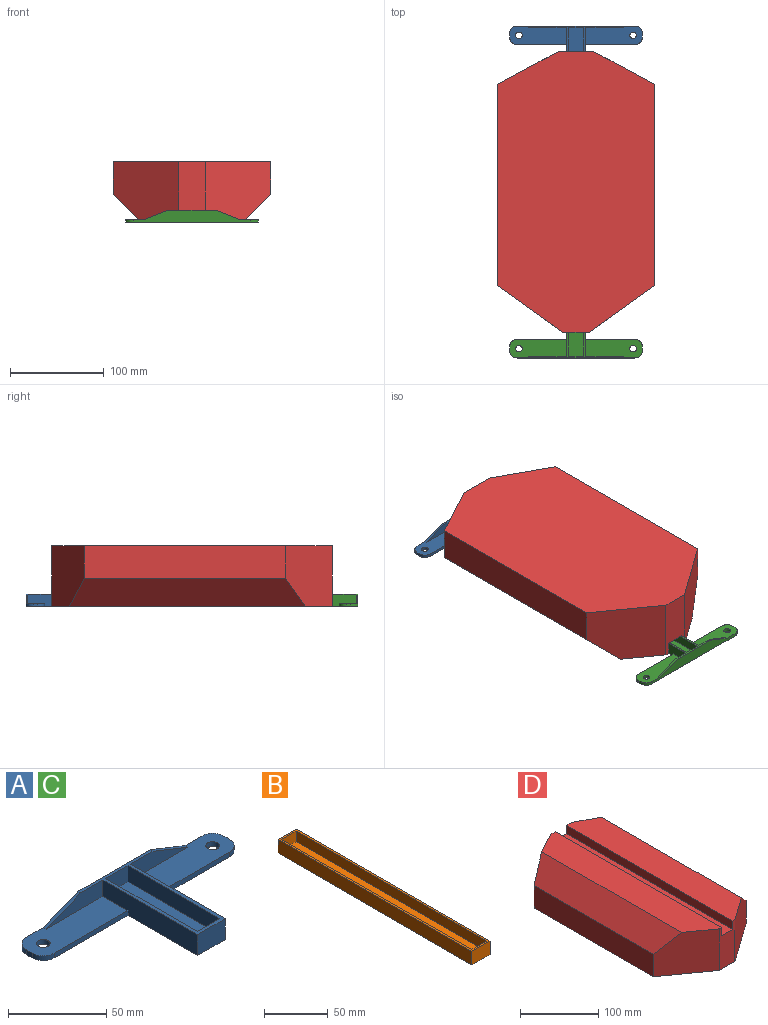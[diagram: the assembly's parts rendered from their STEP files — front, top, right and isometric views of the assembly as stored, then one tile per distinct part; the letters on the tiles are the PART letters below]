
ASSEMBLY  parts=4 mates=3
PART A: 27 faces, bbox 142x70x13 mm
  f0: plane 61x20mm, normal (0,0,1), area 1072mm2, adj f4,f5,f6,f7,f10,f15,f16,f18
  f1: plane 53x3mm, normal (0,-1,0), area 159mm2, adj f2,f11,f12,f14
  f2: plane 68x13mm, normal (-1,0,0), area 830mm2, adj f1,f3,f11,f12,f17,f23
  f3: plane 20x13mm, normal (0,-1,0), area 260mm2, adj f2,f4,f12,f23
  f4: plane 68x13mm, normal (1,0,0), area 830mm2, adj f0,f3,f5,f12,f18,f23
  f5: plane 53x3mm, normal (0,-1,0), area 159mm2, adj f0,f4,f12,f15
  f6: plane 4x3mm, normal (1,0,0), area 12mm2, adj f0,f12,f15,f16
  f7: plane 126x13mm, normal (0,1,0), area 1148mm2, adj f0,f11,f12,f13,f16,f23,f25,f26
  f8: cylinder r=3.5mm len=7mm, axis (0,0,-1), area 66mm2, adj f11,f12
  f9: plane 4x3mm, normal (-1,0,0), area 12mm2, adj f11,f12,f13,f14
  f10: cylinder r=3.5mm len=7mm, axis (0,0,-1), area 66mm2, adj f0,f12
  f11: plane 61x20mm, normal (0,0,1), area 1072mm2, adj f1,f2,f7,f8,f9,f13,f14,f17
  f12: plane 142x70mm, normal (0,0,-1), area 3708.1mm2, adj f1,f2,f3,f4,f5,f6,f7,f8
  f13: cylinder r=8mm len=8mm, axis (0,0,-1), area 37.7mm2, adj f7,f9,f11,f12
  f14: cylinder r=8mm len=8mm, axis (0,0,1), area 37.7mm2, adj f1,f9,f11,f12
  f15: cylinder r=8mm len=8mm, axis (0,0,1), area 37.7mm2, adj f0,f5,f6,f12
  f16: cylinder r=8mm len=8mm, axis (0,0,1), area 37.7mm2, adj f0,f6,f7,f12
  f17: plane 41x10mm, normal (0,-1,0), area 285mm2, adj f2,f11,f23,f26
  f18: plane 41x10mm, normal (0,-1,0), area 285mm2, adj f0,f4,f23,f25
  f19: plane 66x10mm, normal (1,0,0), area 660mm2, adj f20,f22,f23,f24
  f20: plane 16x10mm, normal (0,-1,0), area 160mm2, adj f19,f21,f23,f24
  f21: plane 66x10mm, normal (-1,0,0), area 660mm2, adj f20,f22,f23,f24
  f22: plane 16x10mm, normal (0,1,0), area 160mm2, adj f19,f21,f23,f24
  f23: plane 70x52mm, normal (0,0,1), area 408mm2, adj f2,f3,f4,f7,f17,f18,f19,f20
  f24: plane 66x16mm, normal (0,0,1), area 1056mm2, adj f19,f20,f21,f22
  f25: plane 25x10mm, normal (0.37,0,0.93), area 53.9mm2, adj f0,f7,f18,f23
  f26: plane 25x10mm, normal (-0.37,0,0.93), area 53.9mm2, adj f7,f11,f17,f23
PART B: 11 faces, bbox 20x215x13 mm
  f0: plane 215x13mm, normal (1,0,0), area 2795mm2, adj f1,f3,f4,f9
  f1: plane 20x13mm, normal (0,1,0), area 260mm2, adj f0,f2,f4,f9
  f2: plane 215x13mm, normal (-1,0,0), area 2795mm2, adj f1,f3,f4,f9
  f3: plane 20x13mm, normal (0,-1,0), area 260mm2, adj f0,f2,f4,f9
  f4: plane 215x20mm, normal (0,0,-1), area 4300mm2, adj f0,f1,f2,f3
  f5: plane 16x10mm, normal (0,-1,0), area 160mm2, adj f6,f8,f9,f10
  f6: plane 211x10mm, normal (-1,0,0), area 2110mm2, adj f5,f7,f9,f10
  f7: plane 16x10mm, normal (0,1,0), area 160mm2, adj f6,f8,f9,f10
  f8: plane 211x10mm, normal (1,0,0), area 2110mm2, adj f5,f7,f9,f10
  f9: plane 215x20mm, normal (0,0,1), area 924mm2, adj f0,f1,f2,f3,f5,f6,f7,f8
  f10: plane 211x16mm, normal (0,0,1), area 3376mm2, adj f5,f6,f7,f8
PART C: same geometry as A
PART D: 16 faces, bbox 168x300x65 mm
  f0: plane 300x168mm, normal (0,0,-1), area 44625mm2, adj f3,f4,f5,f6,f12,f13,f14,f15
  f1: plane 300x44mm, normal (0,0,1), area 12298.8mm2, adj f2,f3,f6,f8,f12,f15
  f2: plane 252.58x30mm, normal (0.71,0,0.71), area 9918.9mm2, adj f1,f4,f12,f15
  f3: plane 65x38mm, normal (0,1,0), area 2210mm2, adj f0,f1,f7,f8,f9,f10,f14,f15
  f4: plane 215x35mm, normal (1,0,0), area 7525mm2, adj f0,f2,f12,f15
  f5: plane 215x35mm, normal (-1,0,0), area 7525mm2, adj f0,f11,f13,f14
  f6: plane 65x28mm, normal (0,-1,0), area 1560mm2, adj f0,f1,f7,f8,f9,f10,f12,f13
  f7: plane 300x44mm, normal (0,0,1), area 12298.8mm2, adj f3,f6,f9,f11,f13,f14
  f8: plane 300x13mm, normal (-1,0,0), area 3900mm2, adj f1,f3,f6,f10
  f9: plane 300x13mm, normal (1,0,0), area 3900mm2, adj f3,f6,f7,f10
  f10: plane 300x20mm, normal (0,0,1), area 6000mm2, adj f3,f6,f8,f9
  f11: plane 252.58x30mm, normal (-0.71,0,0.71), area 9918.9mm2, adj f5,f7,f13,f14
  f12: plane 70x65mm, normal (0.58,-0.81,0), area 5038.5mm2, adj f0,f1,f2,f4,f6
  f13: plane 70x65mm, normal (-0.58,-0.81,0), area 5038.5mm2, adj f0,f5,f6,f7,f11
  f14: plane 65x65mm, normal (-0.47,0.88,0), area 4287.5mm2, adj f0,f3,f5,f7,f11
  f15: plane 65x65mm, normal (0.47,0.88,0), area 4287.5mm2, adj f0,f1,f2,f3,f4
PLACE A at identity
PLACE B at identity
PLACE C rot(axis=(0,0,1),180deg) t=(0,0,0)mm
PLACE D rot(axis=(0,1,0),180deg) t=(0,0,65)mm
MATE fastened C.f2 <-> B.f0  axis (-1,0,0) through (10,-107.5,13)mm
MATE fastened D.f7 <-> B.f4  axis (0,0,-1) through (10,0,0)mm
MATE fastened A.f4 <-> B.f0  axis (1,0,0) through (10,107.5,13)mm
